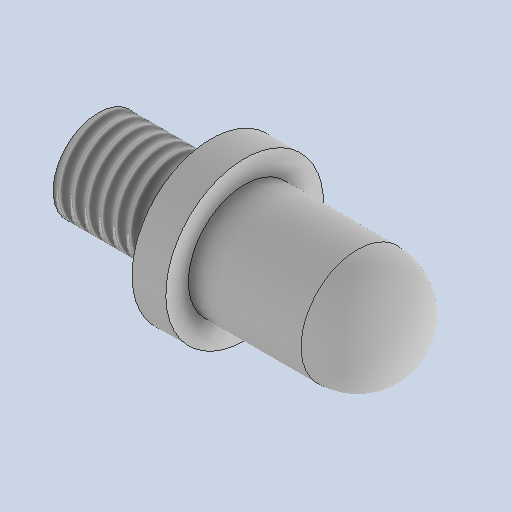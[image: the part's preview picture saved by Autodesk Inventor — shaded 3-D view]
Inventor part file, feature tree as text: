
AUTODESK INVENTOR PART (.ipt)
format: ipt  version: 2025.1 (Build 291241000, 241)  size: 149,504 bytes
history: native  units: mm
features: other x3, sketch x2
ambient origin geometry x8: Origin, YZ Plane, XZ Plane, XY Plane, X Axis, Y Axis, Z Axis, Center Point
bodies: Volumenkörper1 (feature_tree)
feature tree (5):
  other  "1156.ipt"
  other  "Volumenkörper1::1156.ipt"
  other  "TaggingFeature1"
  sketch  "Skizze1"  dims[d0=10.0mm]
  sketch  "Skizze2"
